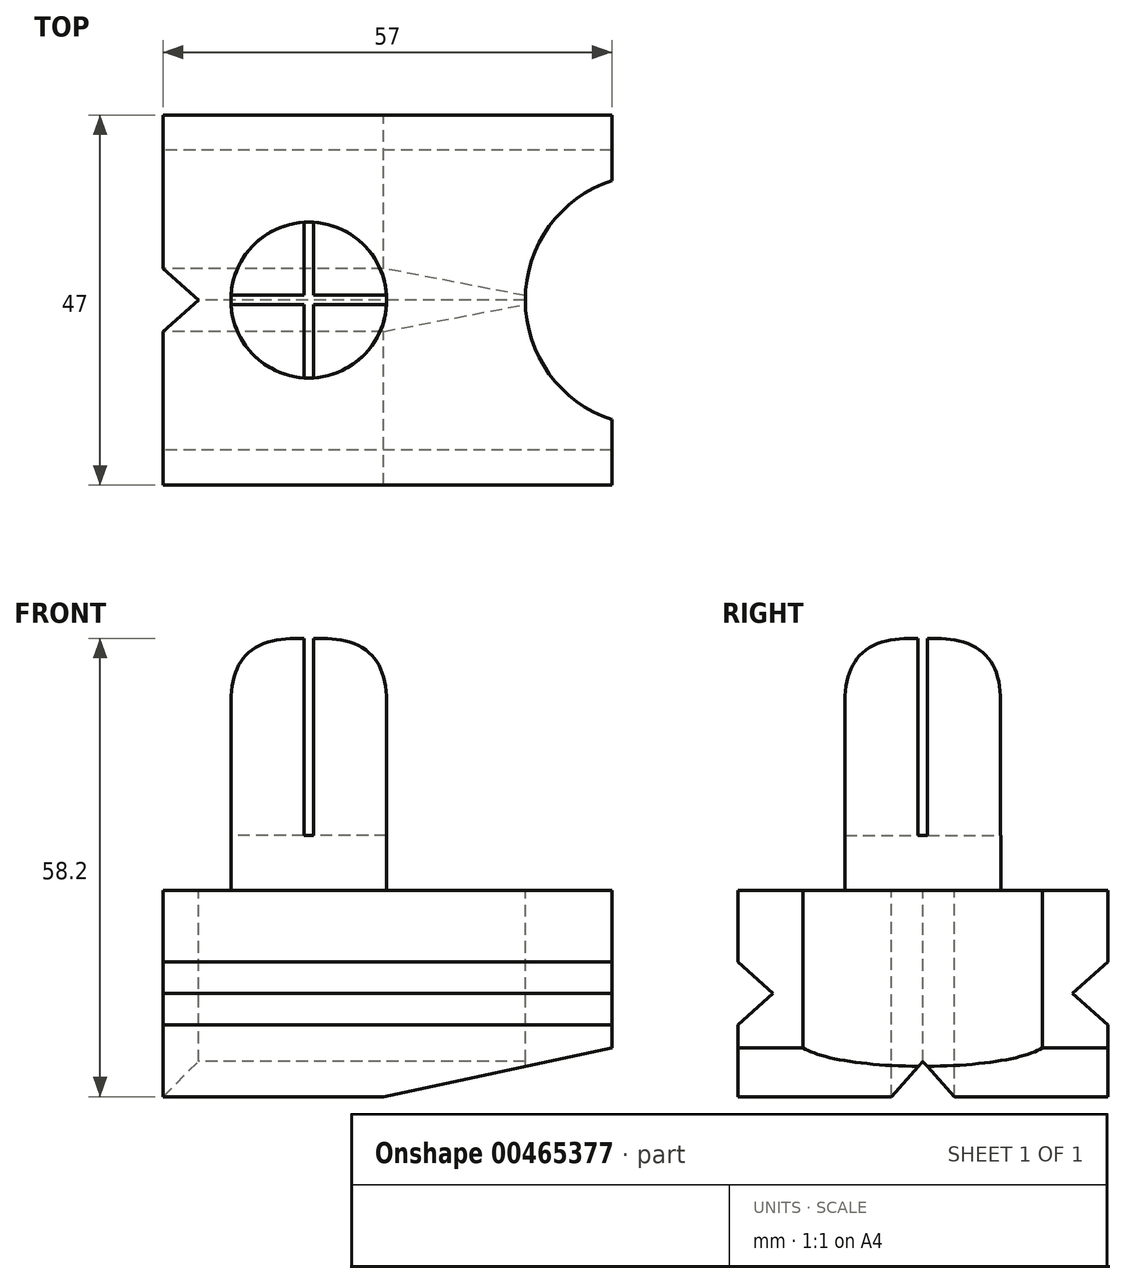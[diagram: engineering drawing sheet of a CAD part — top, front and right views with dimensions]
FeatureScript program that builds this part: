
annotation { "Feature Type Name" : "Feature", "Feature Type Description" : "" }
export const myFeature = defineFeature(function(context is Context, id is Id, definition is map)
    precondition{}
    {
        {
            var Q0;
            Q0=qCreatedBy(makeId("Top.planeOp"),FACE);
            var sketch = newSketch(context, id + "F0", { "sketchPlane" : qUnion([Q0])});
            skLineSegment(sketch, "E0.bottom", {"start": v(18.5, -23.5) * mm, "end": v(-18.5, -23.5) * mm});
            skLineSegment(sketch, "E0.top", {"start": v(18.5, 23.5) * mm, "end": v(-18.5, 23.5) * mm});
            skLineSegment(sketch, "E0.left", {"start": v(18.5, -23.5) * mm, "end": v(18.5, 23.5) * mm});
            skLineSegment(sketch, "E0.right", {"start": v(-18.5, -23.5) * mm, "end": v(-18.5, 23.5) * mm});
            skPoint(sketch, "E0.middle", {"position": v(0, 0) * mm});
            skCircle(sketch, "E1", {"center": v(0, 0) * mm, "radius": 9.9 * mm});
            skSolve(sketch);
        }
        {
            var Q0;
            Q0=makeQuery(id+"F0.imprint","IMPRINT",FACE,{"disambiguationData":[TD([[makeQuery(id+"F0.imprint","IMPRINT",EDGE,{"derivedFrom":sQuery(id+"F0.wireOp",EDGE,"E1")}),1.0]])]});
            extrude(context, id + "F1", {"entities" : qUnion([Q0]), "depth" : 32 * mm});
        }
        {
            var Q0;
            Q0=makeQuery(id+"F0.imprint","IMPRINT",FACE,{"disambiguationData":[TD([[makeQuery(id+"F0.imprint","IMPRINT",EDGE,{"derivedFrom":sQuery(id+"F0.wireOp",EDGE,"E0.bottom")}),-1.0]])]});
            var Q1;
            Q1=makeQuery(id+"F0.imprint","IMPRINT",FACE,{"disambiguationData":[TD([[makeQuery(id+"F0.imprint","IMPRINT",EDGE,{"derivedFrom":sQuery(id+"F0.wireOp",EDGE,"E1")}),1.0]])]});
            extrude(context, id + "F2", {"entities" : qUnion([Q0, Q1]), "operationType" : NewBodyOperationType.ADD, "oppositeDirection" : true, "depth" : 26.2 * mm});
        }
        {
            var Q0;
            Q0=makeQuery(id+"F2.opExtrude","SWEPT_FACE",FACE,{"disambiguationData":[OSD([sQuery(id+"F0.wireOp",EDGE,"E0.left")])]});
            extrude(context, id + "F3", {"entities" : qUnion([Q0]), "operationType" : NewBodyOperationType.ADD, "depth" : 20 * mm});
        }
        {
            var Q0;
            Q0=makeQuery(id+"F1.opExtrude","CAP_EDGE",EDGE,{"disambiguationData":[OSD([sQuery(id+"F0.wireOp",EDGE,"E1")])],"isStart":false});
            fillet(context, id + "F4", {"entities" : qUnion([Q0]), "radius" : 8 * mm, "tangentPropagation" : true, "rho" : 0.5, "crossSection" : FilletCrossSection.CONIC, "allowEdgeOverflow" : false});
        }
        {
            var Q0;
            {var subQ0=sQuery(id+"F0.wireOp",EDGE,"E0.left");Q0=makeQuery(id+"F3.boolean.opBoolean","MERGE",FACE,{"derivedFrom":[makeQuery(id+"F2.opExtrude","CAP_FACE",FACE,{"disambiguationData":[OSD([sQuery(id+"F0.wireOp",EDGE,"E0.bottom"),sQuery(id+"F0.wireOp",EDGE,"E0.top"),subQ0,sQuery(id+"F0.wireOp",EDGE,"E0.right")])],"isStart":true}),makeQuery(id+"F3.opExtrude","SWEPT_FACE",FACE,{"disambiguationData":[OSD([subQ0]),TDD([makeQuery(id+"F2.opExtrude","CAP_EDGE",EDGE,{"disambiguationData":[OSD([subQ0])],"isStart":true})])]})]});}
            var sketch = newSketch(context, id + "F5", { "sketchPlane" : qUnion([Q0])});
            skCircle(sketch, "E2", {"center": v(43.5, 0) * mm, "radius": 16 * mm});
            skSolve(sketch);
        }
        {
            var Q0;
            {var subQ0=sQuery(id+"F5.wireOp",EDGE,"E2");var subQ1=sQuery(id+"F0.wireOp",EDGE,"E0.left");var subQ2=makeQuery(id+"F3.opExtrude","CAP_EDGE",EDGE,{"disambiguationData":[OSD([subQ1]),TDD([makeQuery(id+"F2.opExtrude","CAP_EDGE",EDGE,{"disambiguationData":[OSD([subQ1])],"isStart":true})])],"isStart":false});var subQ3=makeQuery(id+"F5.imprint","INTERSECT",VERTEX,{"disambiguationData":[OD(0.0)],"derivedFrom":[subQ2,subQ0]});Q0=makeQuery(id+"F5.imprint","IMPRINT",FACE,{"disambiguationData":[TD([[makeQuery(id+"F5.imprint","IMPRINT",EDGE,{"disambiguationData":[TD([[subQ3,1.0]])],"derivedFrom":subQ0}),1.0]])]});}
            extrude(context, id + "F6", {"entities" : qUnion([Q0]), "operationType" : NewBodyOperationType.REMOVE, "endBound" : BoundingType.THROUGH_ALL, "oppositeDirection" : true, "depth" : 25 * mm});
        }
        {
            var Q0;
            {var subQ1=sQuery(id+"F0.wireOp",EDGE,"E0.top");var subQ2=sQuery(id+"F0.wireOp",EDGE,"E0.right");Q0=makeQuery(id+"FCS6urC5TY2NgVd_1.boolean.opBoolean","SPLIT",FACE,{"disambiguationData":[TD([makeQuery(id+"F2.opExtrude","SWEPT_FACE",FACE,{"disambiguationData":[OSD([subQ1])]})])],"derivedFrom":makeQuery(id+"F2.opExtrude","SWEPT_FACE",FACE,{"disambiguationData":[OSD([subQ2])]})});}
            var sketch = newSketch(context, id + "F7", { "sketchPlane" : qUnion([Q0])});
            skLineSegment(sketch, "E3", {"start": v(-23.5, -13.1) * mm, "end": v(23.5, -13.1) * mm, "construction": true});
            skLineSegment(sketch, "E4", {"start": v(-19.03, -13.1) * mm, "end": v(-23.5, -17.1) * mm});
            skLineSegment(sketch, "E5", {"start": v(-23.5, -17.1) * mm, "end": v(-23.5, -9.1) * mm});
            skLineSegment(sketch, "E6", {"start": v(-23.5, -9.1) * mm, "end": v(-19.03, -13.1) * mm});
            skLineSegment(sketch, "E7.MirrorCS", {"start": v(23.5, -17.1) * mm, "end": v(23.5, -9.1) * mm});
            skLineSegment(sketch, "E8.MirrorCS", {"start": v(23.5, -9.1) * mm, "end": v(19.03, -13.1) * mm});
            skLineSegment(sketch, "E9.MirrorCS", {"start": v(19.03, -13.1) * mm, "end": v(23.5, -17.1) * mm});
            skSolve(sketch);
        }
        {
            var Q0;
            Q0=makeQuery(id+"F7.imprint","IMPRINT",FACE,{"disambiguationData":[TD([[makeQuery(id+"F7.imprint","IMPRINT",EDGE,{"derivedFrom":sQuery(id+"F7.wireOp",EDGE,"E4")}),-1.0]])]});
            var Q1;
            Q1=makeQuery(id+"F7.imprint","IMPRINT",FACE,{"disambiguationData":[TD([[makeQuery(id+"F7.imprint","IMPRINT",EDGE,{"derivedFrom":sQuery(id+"F7.wireOp",EDGE,"E7.MirrorCS")}),1.0]])]});
            extrude(context, id + "F8", {"entities" : qUnion([Q0, Q1]), "operationType" : NewBodyOperationType.REMOVE, "endBound" : BoundingType.THROUGH_ALL, "oppositeDirection" : true, "depth" : 25 * mm});
        }
        {
            var Q0;
            Q0=makeQuery(id+"F0.imprint","IMPRINT",FACE,{"disambiguationData":[TD([[makeQuery(id+"F0.imprint","IMPRINT",EDGE,{"derivedFrom":sQuery(id+"F0.wireOp",EDGE,"E0.bottom")}),-1.0]])]});
            var sketch = newSketch(context, id + "F9", { "sketchPlane" : qUnion([Q0])});
            skLineSegment(sketch, "E10", {"start": v(-14.03, 0) * mm, "end": v(-18.5, 4) * mm});
            skLineSegment(sketch, "E11", {"start": v(-18.5, 4) * mm, "end": v(-18.5, -4) * mm});
            skLineSegment(sketch, "E12", {"start": v(-18.5, -4) * mm, "end": v(-14.03, 0) * mm});
            skSolve(sketch);
        }
        {
            var Q0;
            Q0=makeQuery(id+"F2.opExtrude","SWEPT_FACE",FACE,{"disambiguationData":[OSD([sQuery(id+"F0.wireOp",EDGE,"E0.right")])]});
            var sketch = newSketch(context, id + "F10", { "sketchPlane" : qUnion([Q0])});
            skLineSegment(sketch, "E13", {"start": v(0, -21.73) * mm, "end": v(-4, -26.2) * mm});
            skLineSegment(sketch, "E14", {"start": v(-4, -26.2) * mm, "end": v(4, -26.2) * mm});
            skLineSegment(sketch, "E15", {"start": v(4, -26.2) * mm, "end": v(0, -21.73) * mm});
            skSolve(sketch);
        }
        {
            var Q0;
            Q0 = qSketchRegion(id + "F10", true);
            extrude(context, id + "F11", {"entities" : qUnion([Q0]), "operationType" : NewBodyOperationType.REMOVE, "endBound" : BoundingType.THROUGH_ALL, "oppositeDirection" : true, "depth" : 25 * mm});
        }
        {
            var Q0;
            Q0=makeQuery(id+"F9.imprint","IMPRINT",FACE,{"disambiguationData":[TD([[makeQuery(id+"F9.imprint","IMPRINT",EDGE,{"derivedFrom":sQuery(id+"F9.wireOp",EDGE,"E10")}),1.0]])]});
            extrude(context, id + "F12", {"entities" : qUnion([Q0]), "operationType" : NewBodyOperationType.REMOVE, "endBound" : BoundingType.THROUGH_ALL, "oppositeDirection" : true, "depth" : 25 * mm});
        }
        {
            var Q0;
            Q0=makeQuery(id+"F1.opExtrude","CAP_FACE",FACE,{"disambiguationData":[OSD([sQuery(id+"F0.wireOp",EDGE,"E1")])],"isStart":false});
            var sketch = newSketch(context, id + "F13", { "sketchPlane" : qUnion([Q0])});
            skLineSegment(sketch, "E16.bottom", {"start": v(0.6, -10.5) * mm, "end": v(-0.6, -10.5) * mm});
            skLineSegment(sketch, "E16.top", {"start": v(0.6, 10.5) * mm, "end": v(-0.6, 10.5) * mm});
            skLineSegment(sketch, "E16.left", {"start": v(0.6, -10.5) * mm, "end": v(0.6, 10.5) * mm});
            skLineSegment(sketch, "E16.right", {"start": v(-0.6, -10.5) * mm, "end": v(-0.6, 10.5) * mm});
            skPoint(sketch, "E16.middle", {"position": v(0, 0) * mm});
            skLineSegment(sketch, "E17.bottom", {"start": v(10.5, -0.6) * mm, "end": v(-10.5, -0.6) * mm});
            skLineSegment(sketch, "E17.top", {"start": v(10.5, 0.6) * mm, "end": v(-10.5, 0.6) * mm});
            skLineSegment(sketch, "E17.left", {"start": v(10.5, -0.6) * mm, "end": v(10.5, 0.6) * mm});
            skLineSegment(sketch, "E17.right", {"start": v(-10.5, -0.6) * mm, "end": v(-10.5, 0.6) * mm});
            skSolve(sketch);
        }
        {
            var Q0;
            Q0 = qSketchRegion(id + "F13", true);
            extrude(context, id + "F14", {"entities" : qUnion([Q0]), "operationType" : NewBodyOperationType.REMOVE, "oppositeDirection" : true, "depth" : 25 * mm});
        }
        {
            var Q0;
            {var subQ0=sQuery(id+"F0.wireOp",EDGE,"E0.left");var subQ2=sQuery(id+"F0.wireOp",EDGE,"E0.top");Q0=makeQuery(id+"F8.boolean.opBoolean","SPLIT",FACE,{"disambiguationData":[TD([makeQuery(id+"F8.opExtrude","SWEPT_FACE",FACE,{"disambiguationData":[OSD([sQuery(id+"F7.wireOp",EDGE,"E4")])]})])],"derivedFrom":makeQuery(id+"F3.boolean.opBoolean","MERGE",FACE,{"derivedFrom":[makeQuery(id+"F2.opExtrude","SWEPT_FACE",FACE,{"disambiguationData":[OSD([subQ2])]}),makeQuery(id+"F3.opExtrude","SWEPT_FACE",FACE,{"disambiguationData":[OSD([subQ2,subQ0])]})]})});}
            var sketch = newSketch(context, id + "F15", { "sketchPlane" : qUnion([Q0])});
            skLineSegment(sketch, "E18", {"start": v(-38.5, -20) * mm, "end": v(-9.5, -26.2) * mm});
            skSolve(sketch);
        }
        {
            var Q0;
            {var subQ0=sQuery(id+"F15.wireOp",EDGE,"E18");Q0=makeQuery(id+"F15.imprint","IMPRINT",FACE,{"disambiguationData":[TD([[makeQuery(id+"F15.imprint","IMPRINT",EDGE,{"derivedFrom":subQ0}),-1.0]])]});}
            extrude(context, id + "F16", {"entities" : qUnion([Q0]), "operationType" : NewBodyOperationType.REMOVE, "endBound" : BoundingType.THROUGH_ALL, "oppositeDirection" : true, "depth" : 25 * mm});
        }
    });
